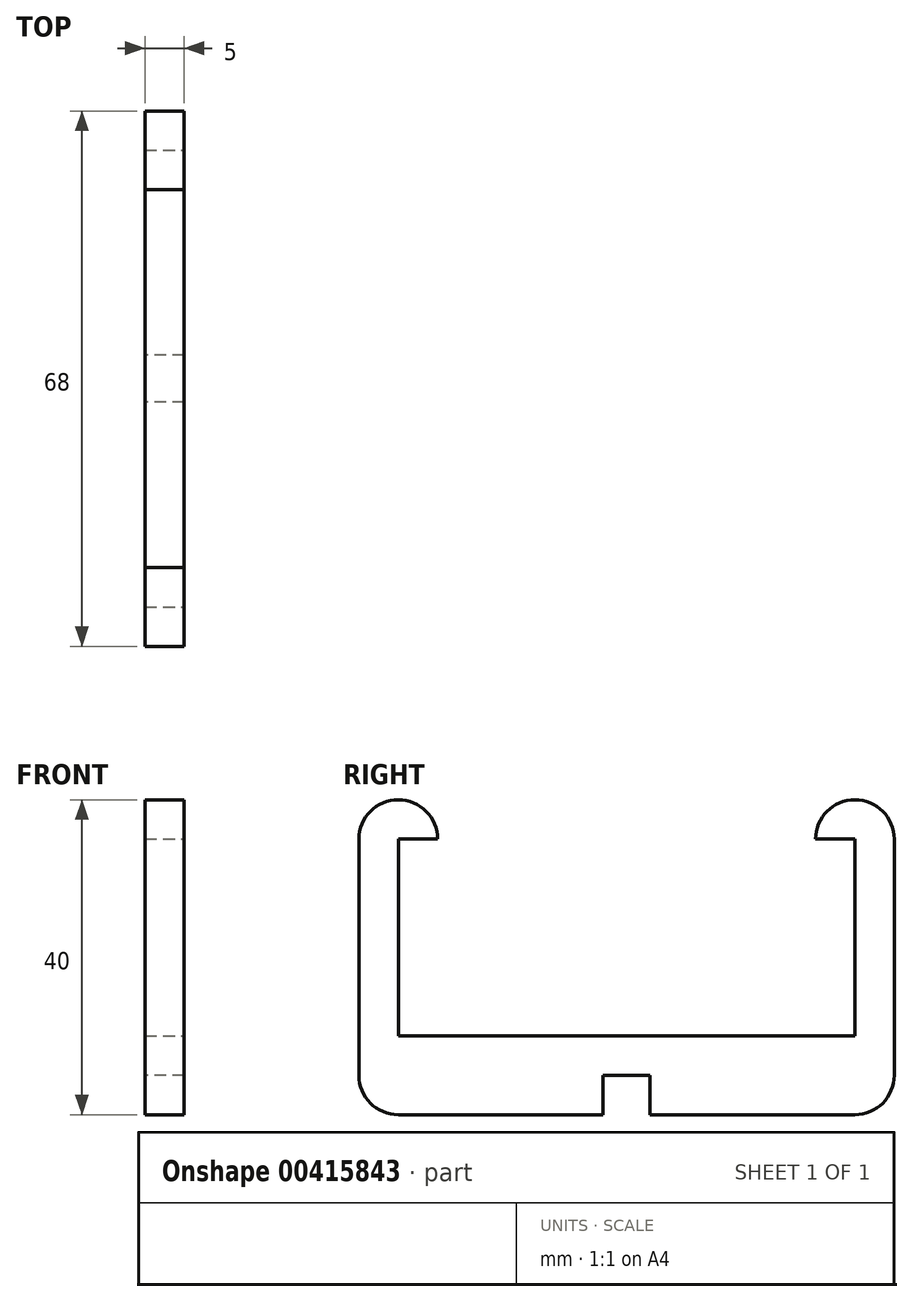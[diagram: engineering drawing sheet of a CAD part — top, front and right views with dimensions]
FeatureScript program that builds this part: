
annotation { "Feature Type Name" : "Feature", "Feature Type Description" : "" }
export const myFeature = defineFeature(function(context is Context, id is Id, definition is map)
    precondition{}
    {
        {
            var Q0;
            Q0=qCreatedBy(makeId("Top.planeOp"),FACE);
            var sketch = newSketch(context, id + "F0", { "sketchPlane" : qUnion([Q0])});
            skLineSegment(sketch, "E0.bottom", {"start": v(2.5, 34) * mm, "end": v(-2.5, 34) * mm});
            skLineSegment(sketch, "E0.top", {"start": v(2.5, -34) * mm, "end": v(-2.5, -34) * mm});
            skLineSegment(sketch, "E0.left", {"start": v(2.5, 34) * mm, "end": v(2.5, -34) * mm});
            skLineSegment(sketch, "E0.right", {"start": v(-2.5, 34) * mm, "end": v(-2.5, -34) * mm});
            skPoint(sketch, "E0.middle", {"position": v(0, 0) * mm});
            skSolve(sketch);
        }
        {
            var Q0;
            Q0=makeQuery(id+"F0.imprint","IMPRINT",FACE,{"disambiguationData":[TD([[makeQuery(id+"F0.imprint","IMPRINT",EDGE,{"derivedFrom":sQuery(id+"F0.wireOp",EDGE,"E0.bottom")}),1.0]])]});
            extrude(context, id + "F1", {"entities" : qUnion([Q0]), "depth" : 10 * mm});
        }
        {
            var Q0;
            Q0=makeQuery(id+"F1.opExtrude","CAP_FACE",FACE,{"disambiguationData":[OSD([sQuery(id+"F0.wireOp",EDGE,"E0.bottom"),sQuery(id+"F0.wireOp",EDGE,"E0.top"),sQuery(id+"F0.wireOp",EDGE,"E0.left"),sQuery(id+"F0.wireOp",EDGE,"E0.right")])],"isStart":false});
            var sketch = newSketch(context, id + "F2", { "sketchPlane" : qUnion([Q0])});
            skLineSegment(sketch, "E1.bottom", {"start": v(-2.5, 34) * mm, "end": v(2.5, 34) * mm});
            skLineSegment(sketch, "E1.top", {"start": v(-2.5, 29) * mm, "end": v(2.5, 29) * mm});
            skLineSegment(sketch, "E1.left", {"start": v(-2.5, 34) * mm, "end": v(-2.5, 29) * mm});
            skLineSegment(sketch, "E1.right", {"start": v(2.5, 34) * mm, "end": v(2.5, 29) * mm});
            skLineSegment(sketch, "E2.MirrorCS", {"start": v(-2.5, -34) * mm, "end": v(2.5, -34) * mm});
            skLineSegment(sketch, "E3.MirrorCS", {"start": v(2.5, -34) * mm, "end": v(2.5, -29) * mm});
            skLineSegment(sketch, "E4.MirrorCS", {"start": v(-2.5, -29) * mm, "end": v(2.5, -29) * mm});
            skLineSegment(sketch, "E5.MirrorCS", {"start": v(-2.5, -34) * mm, "end": v(-2.5, -29) * mm});
            skSolve(sketch);
        }
        {
            var Q0;
            Q0 = qSketchRegion(id + "F2", true);
            extrude(context, id + "F3", {"entities" : qUnion([Q0]), "operationType" : NewBodyOperationType.ADD, "depth" : 30 * mm});
        }
        {
            var Q0;
            Q0=makeQuery(id+"F3.opExtrude","SWEPT_FACE",FACE,{"disambiguationData":[OSD([sQuery(id+"F2.wireOp",EDGE,"E1.top")])]});
            var sketch = newSketch(context, id + "F4", { "sketchPlane" : qUnion([Q0])});
            skLineSegment(sketch, "E6.bottom", {"start": v(-2.5, 40) * mm, "end": v(2.5, 40) * mm});
            skLineSegment(sketch, "E6.top", {"start": v(-2.5, 35) * mm, "end": v(2.5, 35) * mm});
            skLineSegment(sketch, "E6.left", {"start": v(-2.5, 40) * mm, "end": v(-2.5, 35) * mm});
            skLineSegment(sketch, "E6.right", {"start": v(2.5, 40) * mm, "end": v(2.5, 35) * mm});
            skSolve(sketch);
        }
        {
            var Q0;
            Q0=makeQuery(id+"F3.opExtrude","SWEPT_FACE",FACE,{"disambiguationData":[OSD([sQuery(id+"F2.wireOp",EDGE,"E4.MirrorCS")])]});
            var sketch = newSketch(context, id + "F5", { "sketchPlane" : qUnion([Q0])});
            skLineSegment(sketch, "E7.bottom", {"start": v(2.5, 40) * mm, "end": v(-2.5, 40) * mm});
            skLineSegment(sketch, "E7.top", {"start": v(2.5, 35) * mm, "end": v(-2.5, 35) * mm});
            skLineSegment(sketch, "E7.left", {"start": v(2.5, 40) * mm, "end": v(2.5, 35) * mm});
            skLineSegment(sketch, "E7.right", {"start": v(-2.5, 40) * mm, "end": v(-2.5, 35) * mm});
            skSolve(sketch);
        }
        {
            var Q0;
            Q0=makeQuery(id+"F5.imprint","IMPRINT",FACE,{"disambiguationData":[TD([[makeQuery(id+"F5.imprint","IMPRINT",EDGE,{"derivedFrom":sQuery(id+"F5.wireOp",EDGE,"E7.bottom")}),1.0]])]});
            extrude(context, id + "F6", {"entities" : qUnion([Q0]), "operationType" : NewBodyOperationType.ADD, "depth" : 5 * mm});
        }
        {
            var Q0;
            Q0=makeQuery(id+"F4.imprint","IMPRINT",FACE,{"disambiguationData":[TD([[makeQuery(id+"F4.imprint","IMPRINT",EDGE,{"derivedFrom":sQuery(id+"F4.wireOp",EDGE,"E6.bottom")}),-1.0]])]});
            extrude(context, id + "F7", {"entities" : qUnion([Q0]), "operationType" : NewBodyOperationType.ADD, "depth" : 5 * mm});
        }
        {
            var Q0;
            Q0=makeQuery(id+"F1.opExtrude","CAP_FACE",FACE,{"disambiguationData":[OSD([sQuery(id+"F0.wireOp",EDGE,"E0.bottom"),sQuery(id+"F0.wireOp",EDGE,"E0.top"),sQuery(id+"F0.wireOp",EDGE,"E0.left"),sQuery(id+"F0.wireOp",EDGE,"E0.right")])],"isStart":true});
            var sketch = newSketch(context, id + "F8", { "sketchPlane" : qUnion([Q0])});
            skLineSegment(sketch, "E8.bottom", {"start": v(2.5, 3) * mm, "end": v(-2.5, 3) * mm});
            skLineSegment(sketch, "E8.top", {"start": v(2.5, -3) * mm, "end": v(-2.5, -3) * mm});
            skLineSegment(sketch, "E8.left", {"start": v(2.5, 3) * mm, "end": v(2.5, -3) * mm});
            skLineSegment(sketch, "E8.right", {"start": v(-2.5, 3) * mm, "end": v(-2.5, -3) * mm});
            skPoint(sketch, "E8.middle", {"position": v(0, 0) * mm});
            skSolve(sketch);
        }
        {
            var Q0;
            Q0=makeQuery(id+"F8.imprint","IMPRINT",FACE,{"disambiguationData":[TD([[makeQuery(id+"F8.imprint","IMPRINT",EDGE,{"derivedFrom":sQuery(id+"F8.wireOp",EDGE,"E8.bottom")}),1.0]])]});
            extrude(context, id + "F9", {"entities" : qUnion([Q0]), "operationType" : NewBodyOperationType.REMOVE, "oppositeDirection" : true, "depth" : 5 * mm});
        }
        {
            var Q0;
            Q0=makeQuery(id+"F7.opExtrude","CAP_EDGE",EDGE,{"disambiguationData":[OSD([sQuery(id+"F4.wireOp",EDGE,"E6.bottom")])],"isStart":false});
            var Q1;
            Q1=makeQuery(id+"F6.opExtrude","CAP_EDGE",EDGE,{"disambiguationData":[OSD([sQuery(id+"F5.wireOp",EDGE,"E7.bottom")])],"isStart":false});
            var Q2;
            Q2=makeQuery(id+"F3.opExtrude","CAP_EDGE",EDGE,{"disambiguationData":[OSD([sQuery(id+"F2.wireOp",EDGE,"E2.MirrorCS")])],"isStart":false});
            fillet(context, id + "F10", {"entities" : qUnion([Q0, Q1, Q2]), "radius" : 5 * mm, "tangentPropagation" : true, "allowEdgeOverflow" : false});
        }
        {
            var Q0;
            Q0=makeQuery(id+"F3.opExtrude","CAP_EDGE",EDGE,{"disambiguationData":[OSD([sQuery(id+"F2.wireOp",EDGE,"E1.bottom")])],"isStart":false});
            var Q1;
            Q1=makeQuery(id+"F1.opExtrude","CAP_EDGE",EDGE,{"disambiguationData":[OSD([sQuery(id+"F0.wireOp",EDGE,"E0.bottom")])],"isStart":true});
            var Q2;
            Q2=makeQuery(id+"F1.opExtrude","CAP_EDGE",EDGE,{"disambiguationData":[OSD([sQuery(id+"F0.wireOp",EDGE,"E0.top")])],"isStart":true});
            fillet(context, id + "F11", {"entities" : qUnion([Q0, Q1, Q2]), "radius" : 5 * mm, "tangentPropagation" : true, "allowEdgeOverflow" : false});
        }
    });
